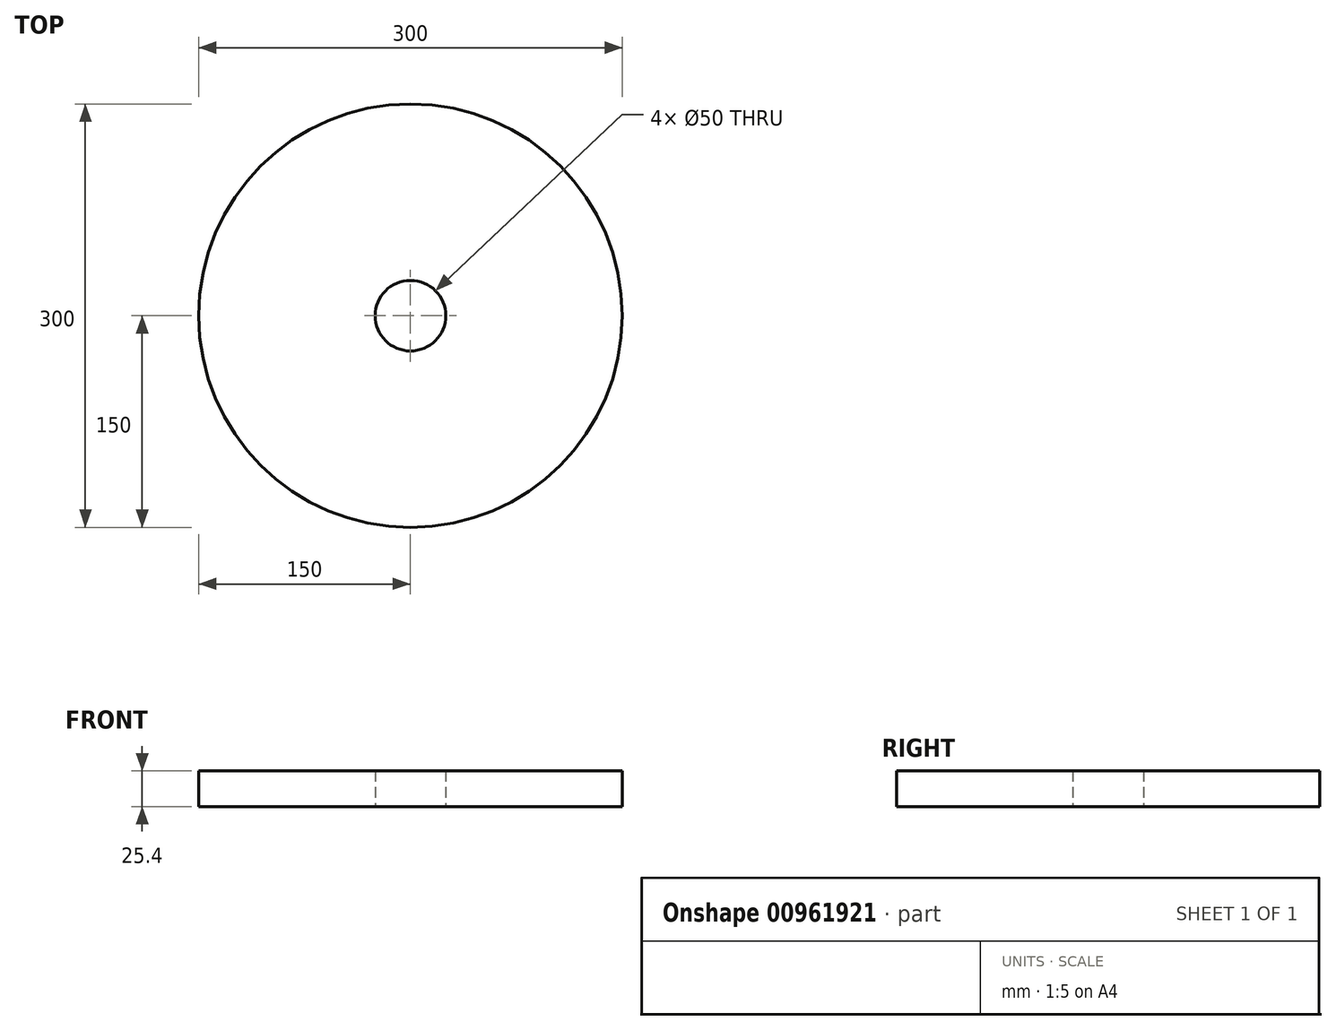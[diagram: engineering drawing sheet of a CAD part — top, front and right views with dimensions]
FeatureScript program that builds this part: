
annotation { "Feature Type Name" : "Feature", "Feature Type Description" : "" }
export const myFeature = defineFeature(function(context is Context, id is Id, definition is map)
    precondition{}
    {
        {
            var Q0;
            Q0=qCreatedBy(makeId("Top.planeOp"),FACE);
            var sketch = newSketch(context, id + "F0", { "sketchPlane" : qUnion([Q0])});
            skCircle(sketch, "E0", {"center": v(0, 0) * mm, "radius": 150 * mm});
            skCircle(sketch, "E1", {"center": v(0, 0) * mm, "radius": 25 * mm});
            skSolve(sketch);
        }
        {
            var Q0;
            Q0=makeQuery(id+"F0.imprint","IMPRINT",FACE,{"disambiguationData":[TD([[makeQuery(id+"F0.imprint","IMPRINT",EDGE,{"derivedFrom":sQuery(id+"F0.wireOp",EDGE,"E0")}),1.0]])]});
            extrude(context, id + "F1", {"entities" : qUnion([Q0]), "depth" : 25.4 * mm, "offsetDistance" : 25 * mm});
        }
    });
